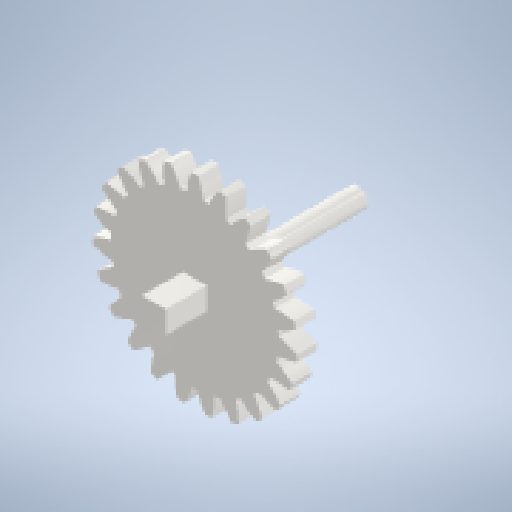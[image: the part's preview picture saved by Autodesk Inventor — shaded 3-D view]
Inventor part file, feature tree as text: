
AUTODESK INVENTOR PART (.ipt)
format: ipt  version: 2023 (Build 270158000, 158)  size: 345,088 bytes
history: native  units: mm (DEFAULTED — no unit token found)
features: sketch x4, extrude x3, plane x3, other x3, projected_geometry x1
ambient origin geometry x8: Origin, YZ Plane, XZ Plane, XY Plane, X Axis, Y Axis, Z Axis, Center Point
bodies: Solid1 (feature_tree)
feature tree (14):
  extrude  "Extrusion1"  Depth=5.0mm TaperAngle=0.0deg
  plane  "Work Plane2"
  plane  "Work Plane8"
  plane  "Work Plane9"
  other  "Spur Gear"
  extrude  "Extrusion2"  Depth=10.0mm TaperAngle=0.0deg
  extrude  "Extrusion3"  Depth=1.36591mm TaperAngle=0.0deg
  sketch  "Sketch1"  dims[d0=50.0mm d1=5.0mm d2=0.0mm]
  sketch  "Sketch2"  dims[d3=46.0mm d4=10.0mm d5=0.0mm]
  other  "Srf1"
  sketch  "Sketch3"  dims[d16=80.0mm d17=0.0mm d34=1.36591mm]
  projected_geometry  "Projected Loop1"
  sketch  "Sketch4"  dims[d39=0.0mm d41=0.0mm d43=80.0mm d46=80.0mm d47=0.0mm d48=0.0mm d49=4.5mm d50=35.0mm d51=0.0mm d52=7.0mm d54=10.0mm d55=0.0mm]
  other  "Pitch Diameter"
